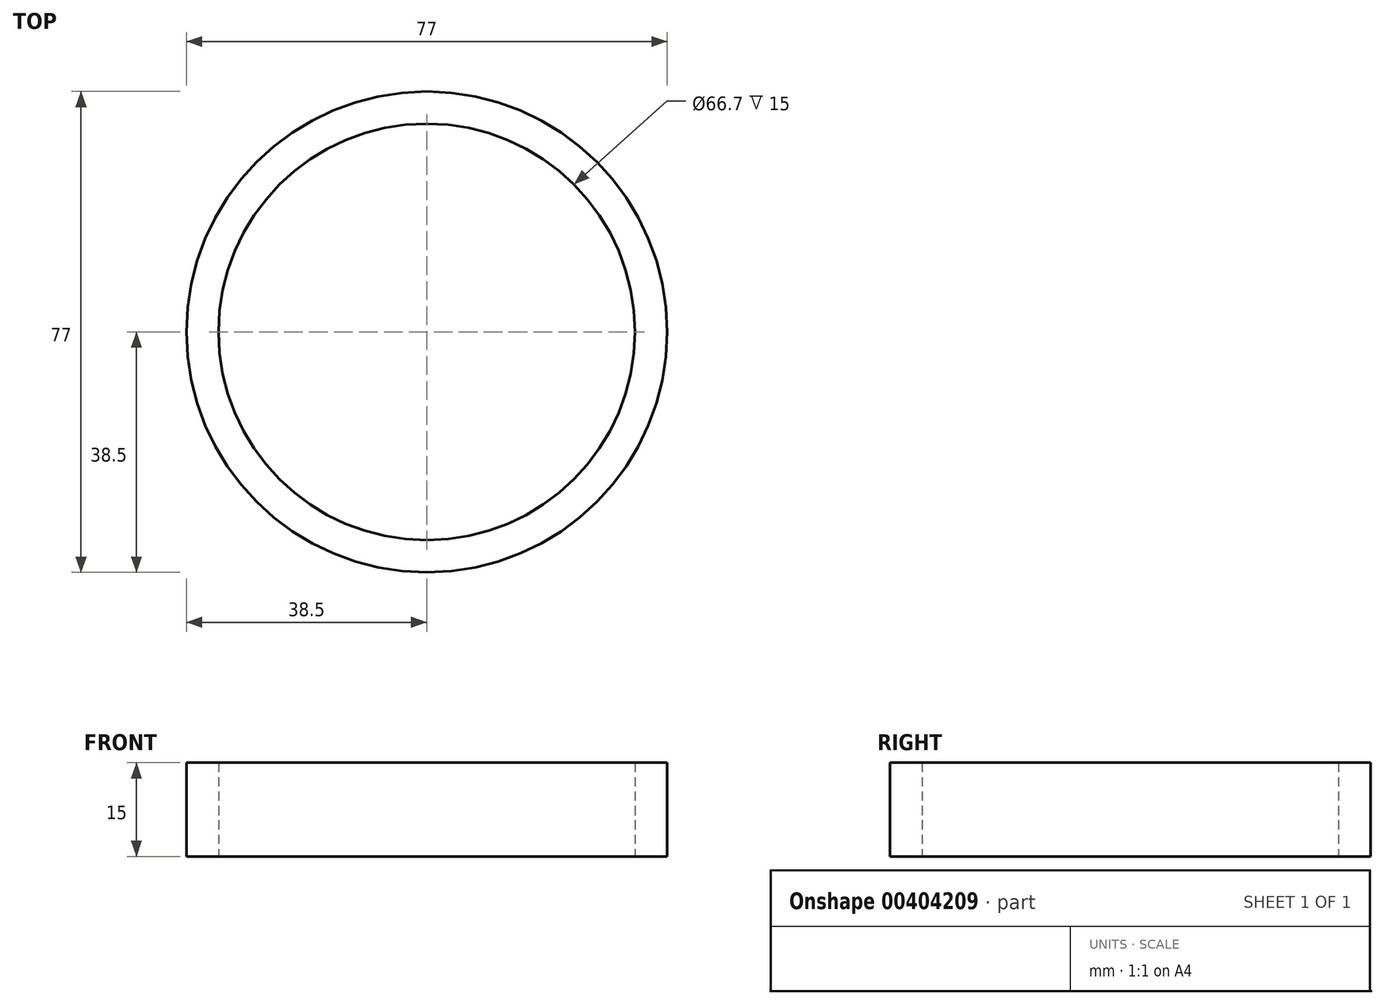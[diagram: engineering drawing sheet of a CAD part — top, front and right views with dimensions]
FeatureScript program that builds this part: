
annotation { "Feature Type Name" : "Feature", "Feature Type Description" : "" }
export const myFeature = defineFeature(function(context is Context, id is Id, definition is map)
    precondition{}
    {
        {
            var Q0;
            Q0=qCreatedBy(makeId("Top.planeOp"),FACE);
            var sketch = newSketch(context, id + "F0", { "sketchPlane" : qUnion([Q0])});
            skCircle(sketch, "E0", {"center": v(0, 0) * mm, "radius": 33.35 * mm});
            skCircle(sketch, "E1", {"center": v(0, 0) * mm, "radius": 38.5 * mm});
            skSolve(sketch);
        }
        {
            var Q0;
            Q0=qSketchRegion(id+"F0",true);
            extrude(context, id + "F1", {"entities" : qUnion([Q0]), "depth" : 15 * mm});
        }
    });
